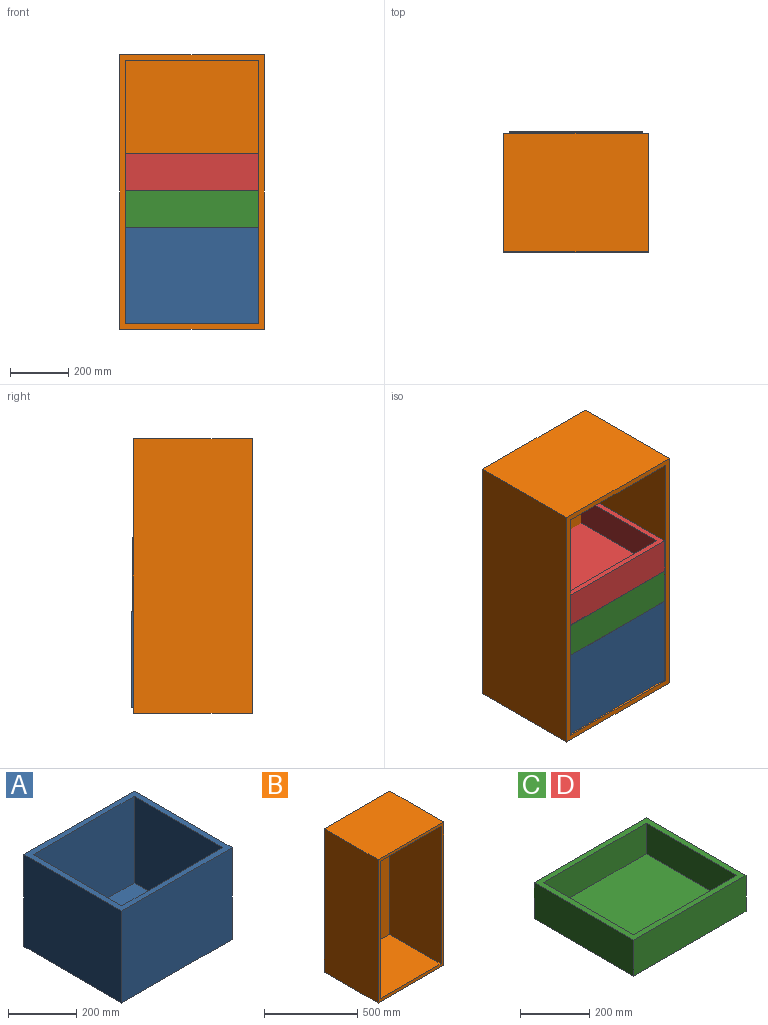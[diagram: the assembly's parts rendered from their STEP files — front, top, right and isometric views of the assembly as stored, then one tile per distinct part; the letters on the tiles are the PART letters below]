
ASSEMBLY  parts=4 mates=6
PART A: 11 faces, bbox 457.2x406.4x330.2 mm
  f0: plane 457.2x406.4mm, normal (0,0,1), area 31451.5mm2, adj f1,f2,f3,f4,f6,f7,f8,f9
  f1: plane 406.4x330.2mm, normal (1,0,0), area 134193.3mm2, adj f0,f2,f4,f5
  f2: plane 457.2x330.2mm, normal (0,1,0), area 150967.4mm2, adj f0,f1,f3,f5
  f3: plane 406.4x330.2mm, normal (-1,0,0), area 134193.3mm2, adj f0,f2,f4,f5
  f4: plane 457.2x330.2mm, normal (0,-1,0), area 150967.4mm2, adj f0,f1,f3,f5
  f5: plane 457.2x406.4mm, normal (0,0,-1), area 185806.1mm2, adj f1,f2,f3,f4
  f6: plane 368.3x311.15mm, normal (-1,0,0), area 114596.5mm2, adj f0,f7,f9,f10
  f7: plane 419.1x311.15mm, normal (0,-1,0), area 130403mm2, adj f0,f6,f8,f10
  f8: plane 368.3x311.15mm, normal (1,0,0), area 114596.5mm2, adj f0,f7,f9,f10
  f9: plane 419.1x311.15mm, normal (0,1,0), area 130403mm2, adj f0,f6,f8,f10
  f10: plane 419.1x368.3mm, normal (0,0,1), area 154354.5mm2, adj f6,f7,f8,f9
PART B: 11 faces, bbox 495.3x406.4x939.8 mm
  f0: plane 939.8x495.3mm, normal (0,-1,0), area 53225.7mm2, adj f1,f2,f3,f4,f6,f7,f8,f9
  f1: plane 939.8x406.4mm, normal (1,0,0), area 381934.7mm2, adj f0,f2,f4,f5
  f2: plane 495.3x406.4mm, normal (0,0,1), area 201289.9mm2, adj f0,f1,f3,f5
  f3: plane 939.8x406.4mm, normal (-1,0,0), area 381934.7mm2, adj f0,f2,f4,f5
  f4: plane 495.3x406.4mm, normal (0,0,-1), area 201289.9mm2, adj f0,f1,f3,f5
  f5: plane 939.8x495.3mm, normal (0,1,0), area 465482.9mm2, adj f1,f2,f3,f4
  f6: plane 901.7x387.35mm, normal (-1,0,0), area 349273.5mm2, adj f0,f7,f9,f10
  f7: plane 457.2x387.35mm, normal (0,0,-1), area 177096.4mm2, adj f0,f6,f8,f10
  f8: plane 901.7x387.35mm, normal (1,0,0), area 349273.5mm2, adj f0,f7,f9,f10
  f9: plane 457.2x387.35mm, normal (0,0,1), area 177096.4mm2, adj f0,f6,f8,f10
  f10: plane 901.7x457.2mm, normal (0,-1,0), area 412257.2mm2, adj f6,f7,f8,f9
PART C: 11 faces, bbox 457.2x406.4x127 mm
  f0: plane 457.2x406.4mm, normal (0,0,1), area 31451.5mm2, adj f1,f2,f3,f4,f6,f7,f8,f9
  f1: plane 406.4x127mm, normal (1,0,0), area 51612.8mm2, adj f0,f2,f4,f5
  f2: plane 457.2x127mm, normal (0,1,0), area 58064.4mm2, adj f0,f1,f3,f5
  f3: plane 406.4x127mm, normal (-1,0,0), area 51612.8mm2, adj f0,f2,f4,f5
  f4: plane 457.2x127mm, normal (0,-1,0), area 58064.4mm2, adj f0,f1,f3,f5
  f5: plane 457.2x406.4mm, normal (0,0,-1), area 185806.1mm2, adj f1,f2,f3,f4
  f6: plane 368.3x107.95mm, normal (-1,0,0), area 39758mm2, adj f0,f7,f9,f10
  f7: plane 419.1x107.95mm, normal (0,-1,0), area 45241.8mm2, adj f0,f6,f8,f10
  f8: plane 368.3x107.95mm, normal (1,0,0), area 39758mm2, adj f0,f7,f9,f10
  f9: plane 419.1x107.95mm, normal (0,1,0), area 45241.8mm2, adj f0,f6,f8,f10
  f10: plane 419.1x368.3mm, normal (0,0,1), area 154354.5mm2, adj f6,f7,f8,f9
PART D: same geometry as C
PLACE A t=(-236.24,-166.55,-505.03)mm
PLACE B t=(-236.24,30.68,-54.18)mm fixed
PLACE C t=(-236.24,-168.45,-174.83)mm
PLACE D t=(-236.24,-169.05,-47.83)mm
MATE planar C.f5 <-> A.f0  axis (0,0,-1) through (-236.24,-168.45,-174.83)mm
MATE planar D.f1 <-> B.f6  axis (1,0,0) through (-7.64,-169.05,-47.83)mm
MATE planar A.f1 <-> B.f6  axis (1,0,0) through (-7.64,-166.55,-339.93)mm
MATE planar C.f1 <-> B.f6  axis (1,0,0) through (-7.64,-168.45,-111.33)mm
MATE planar B.f9 <-> A.f5  axis (0,0,1) through (-236.24,-182.04,-505.03)mm
MATE planar D.f5 <-> C.f0  axis (0,0,-1) through (-236.24,-169.05,-47.83)mm
